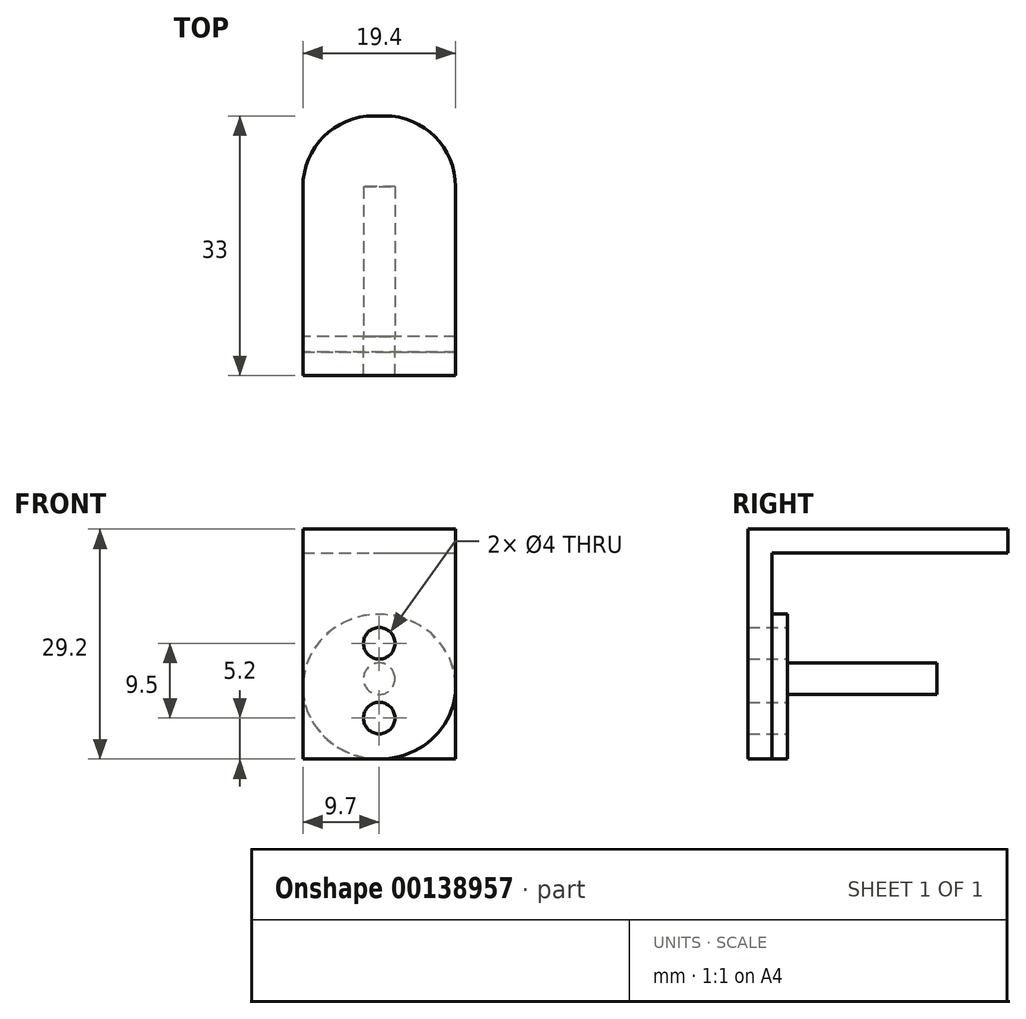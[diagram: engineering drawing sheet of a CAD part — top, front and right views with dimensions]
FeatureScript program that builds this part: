
annotation { "Feature Type Name" : "Feature", "Feature Type Description" : "" }
export const myFeature = defineFeature(function(context is Context, id is Id, definition is map)
    precondition{}
    {
        {
            var Q0;
            Q0=qCreatedBy(makeId("Front.planeOp"),FACE);
            var sketch = newSketch(context, id + "F0", { "sketchPlane" : qUnion([Q0])});
            skEllipse(sketch, "E0", {"center": v(0, 0) * mm, "majorRadius": 9.7 * mm, "minorRadius": 9.2 * mm, "majorAxis": v(1, 0)});
            skCircle(sketch, "E1", {"center": v(0, 1) * mm, "radius": 2 * mm});
            skCircle(sketch, "E2", {"center": v(0, 5.5) * mm, "radius": 2 * mm});
            skCircle(sketch, "E3", {"center": v(0, -4) * mm, "radius": 2 * mm});
            skLineSegment(sketch, "E4.bottom", {"start": v(-9.7, 20) * mm, "end": v(9.7, 20) * mm});
            skLineSegment(sketch, "E4.top", {"start": v(-9.7, -9.2) * mm, "end": v(9.7, -9.2) * mm});
            skLineSegment(sketch, "E4.left", {"start": v(-9.7, 20) * mm, "end": v(-9.7, -9.2) * mm});
            skLineSegment(sketch, "E4.right", {"start": v(9.7, 20) * mm, "end": v(9.7, -9.2) * mm});
            skLineSegment(sketch, "E5", {"start": v(-9.7, 17) * mm, "end": v(9.7, 17) * mm});
            skSolve(sketch);
        }
        {
            var Q0;
            {var subQ0=sQuery(id+"F0.wireOp",EDGE,"E4.bottom");Q0=makeQuery(id+"F0.imprint","IMPRINT",FACE,{"disambiguationData":[TD([[makeQuery(id+"F0.imprint","IMPRINT",EDGE,{"derivedFrom":subQ0}),-1.0]])]});}
            extrude(context, id + "F1", {"entities" : qUnion([Q0]), "oppositeDirection" : true, "depth" : 30 * mm});
        }
        {
            var Q0;
            {var subQ5=sQuery(id+"F0.wireOp",EDGE,"E5");Q0=makeQuery(id+"F0.imprint","IMPRINT",FACE,{"disambiguationData":[TD([[makeQuery(id+"F0.imprint","IMPRINT",EDGE,{"derivedFrom":subQ5}),-1.0]])]});}
            var Q1;
            {var subQ0=sQuery(id+"F0.wireOp",EDGE,"E4.bottom");Q1=makeQuery(id+"F0.imprint","IMPRINT",FACE,{"disambiguationData":[TD([[makeQuery(id+"F0.imprint","IMPRINT",EDGE,{"derivedFrom":subQ0}),-1.0]])]});}
            var Q2;
            {var subQ0=sQuery(id+"F0.wireOp",EDGE,"E4.right");var subQ1=sQuery(id+"F0.wireOp",EDGE,"E0");var subQ2=makeQuery(id+"F0.imprint","INTERSECT",VERTEX,{"derivedFrom":[subQ1,subQ0]});Q2=makeQuery(id+"F0.imprint","IMPRINT",FACE,{"disambiguationData":[TD([[makeQuery(id+"F0.imprint","IMPRINT",EDGE,{"disambiguationData":[TD([[subQ2,1.0]])],"derivedFrom":subQ1}),-1.0]])]});}
            var Q3;
            {var subQ0=sQuery(id+"F0.wireOp",EDGE,"E4.left");var subQ1=sQuery(id+"F0.wireOp",EDGE,"E0");var subQ2=makeQuery(id+"F0.imprint","INTERSECT",VERTEX,{"derivedFrom":[subQ1,subQ0]});Q3=makeQuery(id+"F0.imprint","IMPRINT",FACE,{"disambiguationData":[TD([[makeQuery(id+"F0.imprint","IMPRINT",EDGE,{"disambiguationData":[TD([[subQ2,-1.0]])],"derivedFrom":subQ1}),-1.0]])]});}
            var Q4;
            Q4=makeQuery(id+"F0.imprint","IMPRINT",FACE,{"disambiguationData":[TD([[makeQuery(id+"F0.imprint","IMPRINT",EDGE,{"derivedFrom":sQuery(id+"F0.wireOp",EDGE,"E1")}),-1.0]])]});
            var Q5;
            Q5=makeQuery(id+"F0.imprint","IMPRINT",FACE,{"disambiguationData":[TD([[makeQuery(id+"F0.imprint","IMPRINT",EDGE,{"derivedFrom":sQuery(id+"F0.wireOp",EDGE,"E1")}),1.0]])]});
            extrude(context, id + "F2", {"entities" : qUnion([Q0, Q1, Q2, Q3, Q4, Q5]), "operationType" : NewBodyOperationType.ADD, "depth" : 3 * mm});
        }
        {
            var Q0;
            Q0=makeQuery(id+"F0.imprint","IMPRINT",FACE,{"disambiguationData":[TD([[makeQuery(id+"F0.imprint","IMPRINT",EDGE,{"derivedFrom":sQuery(id+"F0.wireOp",EDGE,"E1")}),-1.0]])]});
            extrude(context, id + "F3", {"entities" : qUnion([Q0]), "operationType" : NewBodyOperationType.ADD, "oppositeDirection" : true, "depth" : 2 * mm});
        }
        {
            var Q0;
            Q0=makeQuery(id+"F0.imprint","IMPRINT",FACE,{"disambiguationData":[TD([[makeQuery(id+"F0.imprint","IMPRINT",EDGE,{"derivedFrom":sQuery(id+"F0.wireOp",EDGE,"E1")}),1.0]])]});
            extrude(context, id + "F4", {"entities" : qUnion([Q0]), "operationType" : NewBodyOperationType.ADD, "oppositeDirection" : true, "depth" : 21 * mm});
        }
        {
            var Q0;
            Q0=makeQuery(id+"F1.opExtrude","CAP_EDGE",EDGE,{"disambiguationData":[OSD([sQuery(id+"F0.wireOp",EDGE,"E4.left")])],"isStart":false});
            var Q1;
            Q1=makeQuery(id+"F1.opExtrude","CAP_EDGE",EDGE,{"disambiguationData":[OSD([sQuery(id+"F0.wireOp",EDGE,"E4.right")])],"isStart":false});
            fillet(context, id + "F5", {"entities" : qUnion([Q0, Q1]), "radius" : 9 * mm, "tangentPropagation" : true, "allowEdgeOverflow" : false});
        }
    });
